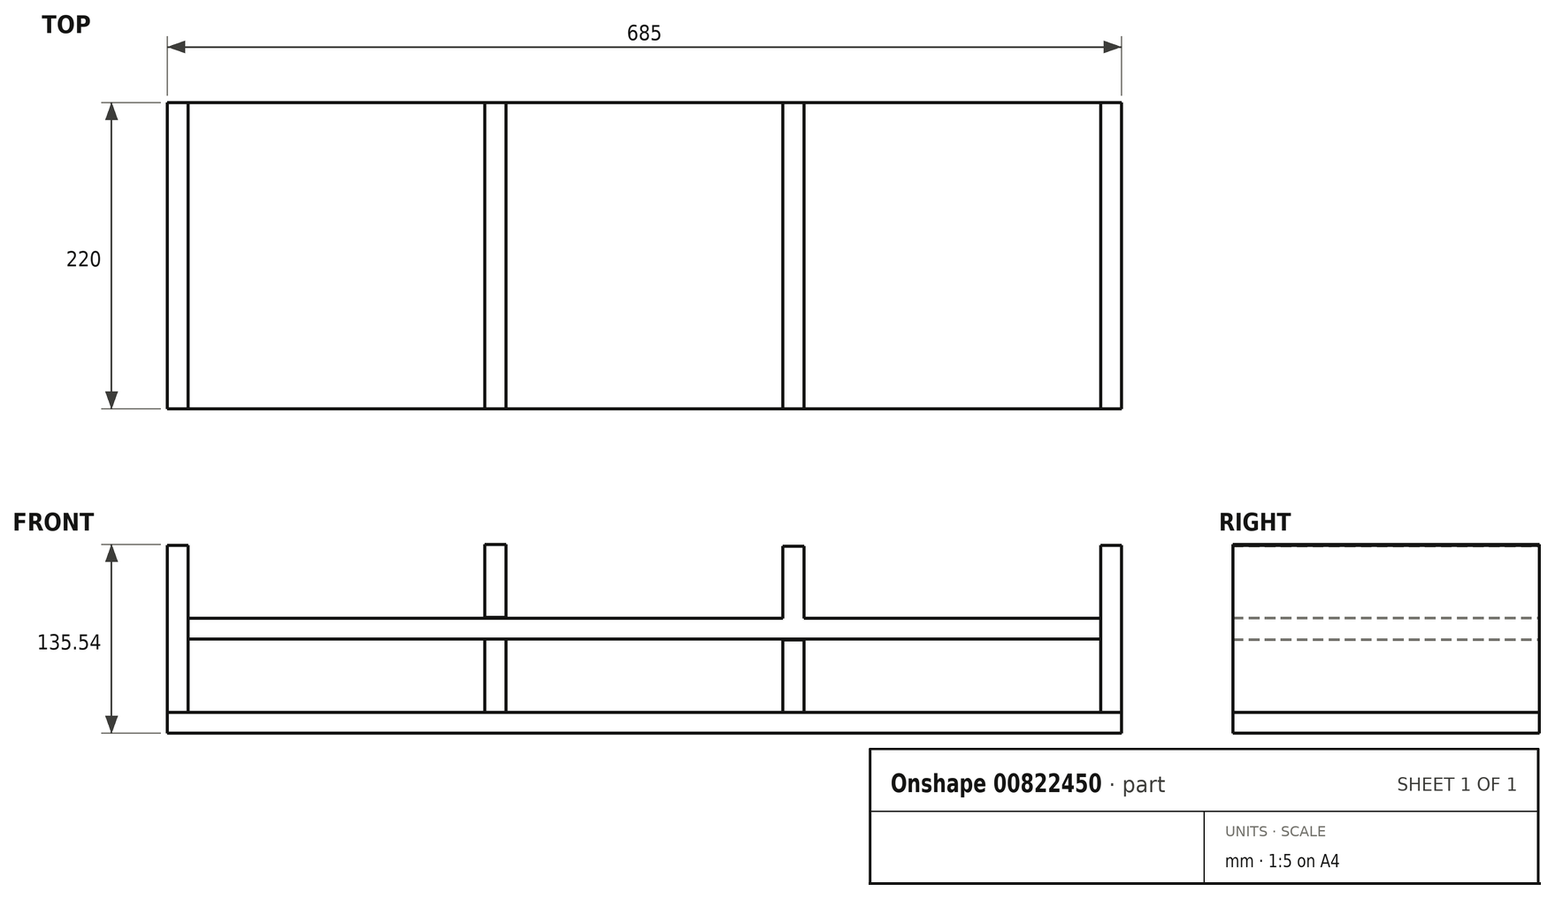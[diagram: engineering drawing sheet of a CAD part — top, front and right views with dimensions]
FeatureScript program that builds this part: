
annotation { "Feature Type Name" : "Feature", "Feature Type Description" : "" }
export const myFeature = defineFeature(function(context is Context, id is Id, definition is map)
    precondition{}
    {
        {
            var Q0;
            Q0=qCreatedBy(makeId("Top.planeOp"),FACE);
            var sketch = newSketch(context, id + "F0", { "sketchPlane" : qUnion([Q0])});
            skLineSegment(sketch, "E0.bottom", {"start": v(-346.3, -20) * mm, "end": v(353.7, -20) * mm});
            skLineSegment(sketch, "E0.top", {"start": v(-346.3, -240) * mm, "end": v(353.7, -240) * mm});
            skLineSegment(sketch, "E0.left", {"start": v(-346.3, -20) * mm, "end": v(-346.3, -240) * mm});
            skLineSegment(sketch, "E0.right", {"start": v(353.7, -20) * mm, "end": v(353.7, -240) * mm});
            skLineSegment(sketch, "E1.bottom", {"start": v(-346.3, -20) * mm, "end": v(-331.3, -20) * mm});
            skLineSegment(sketch, "E1.top", {"start": v(-346.3, -240) * mm, "end": v(-331.3, -240) * mm});
            skLineSegment(sketch, "E1.right", {"start": v(-331.3, -20) * mm, "end": v(-331.3, -240) * mm});
            skSolve(sketch);
        }
        {
            var Q0;
            {var subQ2=sQuery(id+"F0.wireOp",EDGE,"E0.right");Q0=makeQuery(id+"F0.imprint","IMPRINT",FACE,{"disambiguationData":[TD([[makeQuery(id+"F0.imprint","IMPRINT",EDGE,{"derivedFrom":subQ2}),-1.0]])]});}
            extrude(context, id + "F1", {"entities" : qUnion([Q0]), "depth" : 15 * mm, "offsetDistance" : 25 * mm});
        }
        {
            var Q0;
            Q0=makeQuery(id+"F1.opExtrude","CAP_FACE",FACE,{"disambiguationData":[OSD([sQuery(id+"F0.wireOp",EDGE,"E0.bottom"),sQuery(id+"F0.wireOp",EDGE,"E0.top"),sQuery(id+"F0.wireOp",EDGE,"E0.right"),sQuery(id+"F0.wireOp",EDGE,"E1.right")])],"isStart":false});
            var sketch = newSketch(context, id + "F2", { "sketchPlane" : qUnion([Q0])});
            skLineSegment(sketch, "E2.bottom", {"start": v(-331.3, -20) * mm, "end": v(-316.3, -20) * mm});
            skLineSegment(sketch, "E2.top", {"start": v(-331.3, -240) * mm, "end": v(-316.3, -240) * mm});
            skLineSegment(sketch, "E2.left", {"start": v(-331.3, -20) * mm, "end": v(-331.3, -240) * mm});
            skLineSegment(sketch, "E2.right", {"start": v(-316.3, -20) * mm, "end": v(-316.3, -240) * mm});
            skSolve(sketch);
        }
        {
            var Q0;
            Q0=makeQuery(id+"F2.imprint","IMPRINT",FACE,{"disambiguationData":[TD([[makeQuery(id+"F2.imprint","IMPRINT",EDGE,{"derivedFrom":sQuery(id+"F2.wireOp",EDGE,"E2.bottom")}),-1.0]])]});
            extrude(context, id + "F3", {"entities" : qUnion([Q0]), "depth" : 120 * mm, "offsetDistance" : 25 * mm});
        }
        {
            var Q0;
            Q0=makeQuery(id+"F1.opExtrude","CAP_FACE",FACE,{"disambiguationData":[OSD([sQuery(id+"F0.wireOp",EDGE,"E0.bottom"),sQuery(id+"F0.wireOp",EDGE,"E0.top"),sQuery(id+"F0.wireOp",EDGE,"E0.right"),sQuery(id+"F0.wireOp",EDGE,"E1.right")])],"isStart":false});
            var sketch = newSketch(context, id + "F4", { "sketchPlane" : qUnion([Q0])});
            skLineSegment(sketch, "E3.bottom", {"start": v(353.7, -20) * mm, "end": v(338.7, -20) * mm});
            skLineSegment(sketch, "E3.top", {"start": v(353.7, -240) * mm, "end": v(338.7, -240) * mm});
            skLineSegment(sketch, "E3.left", {"start": v(353.7, -20) * mm, "end": v(353.7, -240) * mm});
            skLineSegment(sketch, "E3.right", {"start": v(338.7, -20) * mm, "end": v(338.7, -240) * mm});
            skSolve(sketch);
        }
        {
            var Q0;
            Q0=makeQuery(id+"F4.imprint","IMPRINT",FACE,{"disambiguationData":[TD([[makeQuery(id+"F4.imprint","IMPRINT",EDGE,{"derivedFrom":sQuery(id+"F4.wireOp",EDGE,"E3.bottom")}),-1.0]])]});
            extrude(context, id + "F5", {"entities" : qUnion([Q0]), "depth" : 120 * mm, "offsetDistance" : 25 * mm});
        }
        {
            var Q0;
            Q0=makeQuery(id+"F3.opExtrude","SWEPT_FACE",FACE,{"disambiguationData":[OSD([sQuery(id+"F2.wireOp",EDGE,"E2.right")])]});
            var sketch = newSketch(context, id + "F6", { "sketchPlane" : qUnion([Q0])});
            skLineSegment(sketch, "E4", {"start": v(-20, 75) * mm, "end": v(-240, 75) * mm, "construction": true});
            skLineSegment(sketch, "E5.bottom", {"start": v(-240, 82.5) * mm, "end": v(-20, 82.5) * mm});
            skLineSegment(sketch, "E5.top", {"start": v(-240, 67.5) * mm, "end": v(-20, 67.5) * mm});
            skLineSegment(sketch, "E5.left", {"start": v(-240, 82.5) * mm, "end": v(-240, 67.5) * mm});
            skLineSegment(sketch, "E5.right", {"start": v(-20, 82.5) * mm, "end": v(-20, 67.5) * mm});
            skSolve(sketch);
        }
        {
            var Q0;
            Q0=makeQuery(id+"F6.imprint","IMPRINT",FACE,{"disambiguationData":[TD([[makeQuery(id+"F6.imprint","IMPRINT",EDGE,{"derivedFrom":sQuery(id+"F6.wireOp",EDGE,"E5.bottom")}),-1.0]])]});
            extrude(context, id + "F7", {"entities" : qUnion([Q0]), "endBound" : BoundingType.UP_TO_NEXT, "depth" : 25 * mm, "offsetDistance" : 25 * mm});
        }
        {
            var Q0;
            Q0=makeQuery(id+"F1.opExtrude","SWEPT_FACE",FACE,{"disambiguationData":[OSD([sQuery(id+"F0.wireOp",EDGE,"E0.bottom")])]});
            var sketch = newSketch(context, id + "F8", { "sketchPlane" : qUnion([Q0])});
            skLineSegment(sketch, "E6.bottom", {"start": v(-125.7, 66.92) * mm, "end": v(-110.7, 66.92) * mm});
            skLineSegment(sketch, "E6.top", {"start": v(-125.7, 15) * mm, "end": v(-110.7, 15) * mm});
            skLineSegment(sketch, "E6.left", {"start": v(-125.7, 66.92) * mm, "end": v(-125.7, 15) * mm});
            skLineSegment(sketch, "E6.right", {"start": v(-110.7, 66.92) * mm, "end": v(-110.7, 15) * mm});
            skLineSegment(sketch, "E7.bottom", {"start": v(88.3, 67.5) * mm, "end": v(103.3, 67.5) * mm});
            skLineSegment(sketch, "E7.top", {"start": v(88.3, 15) * mm, "end": v(103.3, 15) * mm});
            skLineSegment(sketch, "E7.left", {"start": v(88.3, 67.5) * mm, "end": v(88.3, 15) * mm});
            skLineSegment(sketch, "E7.right", {"start": v(103.3, 67.5) * mm, "end": v(103.3, 15) * mm});
            skSolve(sketch);
        }
        {
            var Q0;
            Q0=makeQuery(id+"F8.imprint","IMPRINT",FACE,{"disambiguationData":[TD([[makeQuery(id+"F8.imprint","IMPRINT",EDGE,{"derivedFrom":sQuery(id+"F8.wireOp",EDGE,"E6.bottom")}),-1.0]])]});
            var Q1;
            Q1=makeQuery(id+"F8.imprint","IMPRINT",FACE,{"disambiguationData":[TD([[makeQuery(id+"F8.imprint","IMPRINT",EDGE,{"derivedFrom":sQuery(id+"F8.wireOp",EDGE,"E7.bottom")}),-1.0]])]});
            extrude(context, id + "F9", {"entities" : qUnion([Q0, Q1]), "oppositeDirection" : true, "depth" : 220 * mm, "offsetDistance" : 25 * mm});
        }
        {
            var Q0;
            Q0=makeQuery(id+"F7.opExtrude","SWEPT_FACE",FACE,{"disambiguationData":[OSD([sQuery(id+"F6.wireOp",EDGE,"E5.right")])]});
            var sketch = newSketch(context, id + "F10", { "sketchPlane" : qUnion([Q0])});
            skLineSegment(sketch, "E8.bottom", {"start": v(-125.7, 134.24) * mm, "end": v(-110.7, 134.24) * mm});
            skLineSegment(sketch, "E8.top", {"start": v(-125.7, 82.33) * mm, "end": v(-110.7, 82.33) * mm});
            skLineSegment(sketch, "E8.left", {"start": v(-125.7, 134.24) * mm, "end": v(-125.7, 82.33) * mm});
            skLineSegment(sketch, "E8.right", {"start": v(-110.7, 134.24) * mm, "end": v(-110.7, 82.33) * mm});
            skLineSegment(sketch, "E9.bottom", {"start": v(88.3, 135.54) * mm, "end": v(103.3, 135.54) * mm});
            skLineSegment(sketch, "E9.top", {"start": v(88.3, 83.04) * mm, "end": v(103.3, 83.04) * mm});
            skLineSegment(sketch, "E9.left", {"start": v(88.3, 135.54) * mm, "end": v(88.3, 83.04) * mm});
            skLineSegment(sketch, "E9.right", {"start": v(103.3, 135.54) * mm, "end": v(103.3, 83.04) * mm});
            skSolve(sketch);
        }
        {
            var Q0;
            {var subQ0=sQuery(id+"F10.wireOp",EDGE,"E8.bottom");Q0=makeQuery(id+"F10.imprint","IMPRINT",FACE,{"disambiguationData":[TD([[makeQuery(id+"F10.imprint","IMPRINT",EDGE,{"derivedFrom":subQ0}),-1.0]])]});}
            var Q1;
            Q1=makeQuery(id+"F10.imprint","IMPRINT",FACE,{"disambiguationData":[TD([[makeQuery(id+"F10.imprint","IMPRINT",EDGE,{"derivedFrom":sQuery(id+"F10.wireOp",EDGE,"E9.bottom")}),-1.0]])]});
            extrude(context, id + "F11", {"entities" : qUnion([Q0, Q1]), "operationType" : NewBodyOperationType.ADD, "oppositeDirection" : true, "depth" : 220 * mm, "offsetDistance" : 25 * mm});
        }
    });
